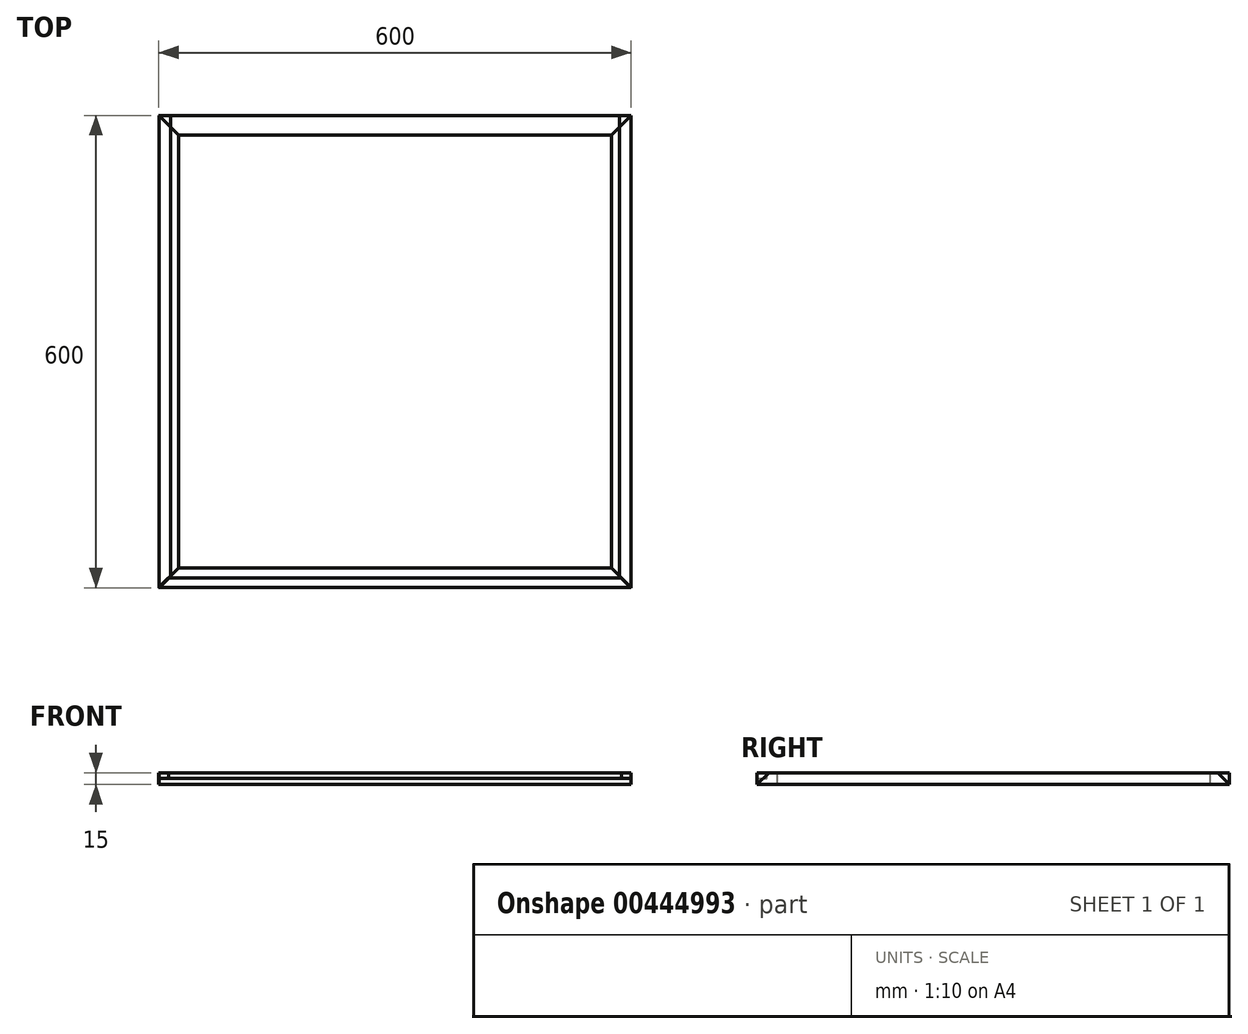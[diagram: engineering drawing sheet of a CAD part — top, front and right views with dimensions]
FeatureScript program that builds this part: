
annotation { "Feature Type Name" : "Feature", "Feature Type Description" : "" }
export const myFeature = defineFeature(function(context is Context, id is Id, definition is map)
    precondition{}
    {
        {
            var Q0;
            Q0=qCreatedBy(makeId("Front.planeOp"),FACE);
            var sketch = newSketch(context, id + "F0", { "sketchPlane" : qUnion([Q0])});
            skLineSegment(sketch, "E0.bottom", {"start": v(0, 0) * mm, "end": v(25, 0) * mm});
            skLineSegment(sketch, "E0.top", {"start": v(0, 15) * mm, "end": v(25, 15) * mm});
            skLineSegment(sketch, "E0.left", {"start": v(0, 0) * mm, "end": v(0, 15) * mm});
            skLineSegment(sketch, "E0.right", {"start": v(25, 0) * mm, "end": v(25, 15) * mm});
            skSolve(sketch);
        }
        {
            var Q0;
            Q0=makeQuery(id+"F0.imprint","IMPRINT",FACE,{"disambiguationData":[TD([[makeQuery(id+"F0.imprint","IMPRINT",EDGE,{"derivedFrom":sQuery(id+"F0.wireOp",EDGE,"E0.bottom")}),1.0]])]});
            extrude(context, id + "F1", {"entities" : qUnion([Q0]), "endBound" : BoundingType.SYMMETRIC, "depth" : 600 * mm});
        }
        {
            var Q0;
            Q0=makeQuery(id+"F1.opExtrude","SWEPT_FACE",FACE,{"disambiguationData":[OSD([sQuery(id+"F0.wireOp",EDGE,"E0.bottom")])]});
            var sketch = newSketch(context, id + "F2", { "sketchPlane" : qUnion([Q0])});
            skLineSegment(sketch, "E1", {"start": v(25, 300) * mm, "end": v(0, 275) * mm});
            skLineSegment(sketch, "E2", {"start": v(0, 275) * mm, "end": v(0, 300) * mm});
            skLineSegment(sketch, "E3", {"start": v(0, 300) * mm, "end": v(25, 300) * mm});
            skLineSegment(sketch, "E4.MirrorCS", {"start": v(25, -300) * mm, "end": v(0, -275) * mm});
            skLineSegment(sketch, "E5.MirrorCS", {"start": v(0, -300) * mm, "end": v(25, -300) * mm});
            skLineSegment(sketch, "E6.MirrorCS", {"start": v(0, -275) * mm, "end": v(0, -300) * mm});
            skSolve(sketch);
        }
        {
            var Q0;
            Q0=makeQuery(id+"F2.imprint","IMPRINT",FACE,{"disambiguationData":[TD([[makeQuery(id+"F2.imprint","IMPRINT",EDGE,{"derivedFrom":sQuery(id+"F2.wireOp",EDGE,"E1")}),-1.0]])]});
            var Q1;
            Q1=makeQuery(id+"F2.imprint","IMPRINT",FACE,{"disambiguationData":[TD([[makeQuery(id+"F2.imprint","IMPRINT",EDGE,{"derivedFrom":sQuery(id+"F2.wireOp",EDGE,"E4.MirrorCS")}),1.0]])]});
            extrude(context, id + "F3", {"entities" : qUnion([Q0, Q1]), "operationType" : NewBodyOperationType.REMOVE, "endBound" : BoundingType.SYMMETRIC, "oppositeDirection" : true, "depth" : 60 * mm});
        }
        {
            var Q0;
            Q0=qCreatedBy(makeId("Front.planeOp"),FACE);
            var sketch = newSketch(context, id + "F4", { "sketchPlane" : qUnion([Q0])});
            skLineSegment(sketch, "E7", {"start": v(-274.97, 0) * mm, "end": v(-274.97, -161.43) * mm, "construction": true});
            skSolve(sketch);
        }
        {
            var Q0;
            Q0=makeQuery(id+"F1.opExtrude","SWEPT_BODY",BODY,{"disambiguationData":[OSD([sQuery(id+"F0.wireOp",EDGE,"E0.bottom"),sQuery(id+"F0.wireOp",EDGE,"E0.top"),sQuery(id+"F0.wireOp",EDGE,"E0.left"),sQuery(id+"F0.wireOp",EDGE,"E0.right")])]});
            var Q1;
            Q1=sQuery(id+"F4.wireOp",EDGE,"E7");
            circularPattern(context, id + "F5", {"entities" : qUnion([Q0]), "axis" : qUnion([Q1]), "angle" : 360 * degree, "instanceCount" : 4, "equalSpace" : true});
        }
        {
            var Q0;
            Q0=makeQuery(id+"F5.opPattern","COPY",FACE,{"derivedFrom":makeQuery(id+"F1.opExtrude","SWEPT_FACE",FACE,{"disambiguationData":[OSD([sQuery(id+"F0.wireOp",EDGE,"E0.left")])]}),"instanceName":"2"});
            var Q1;
            Q1=makeQuery(id+"F1.opExtrude","SWEPT_FACE",FACE,{"disambiguationData":[OSD([sQuery(id+"F0.wireOp",EDGE,"E0.left")])]});
            extrude(context, id + "F6", {"entities" : qUnion([Q0]), "endBound" : BoundingType.UP_TO_SURFACE, "endBoundEntityFace" : qUnion([Q1]), "depth" : 25 * mm});
        }
        {
            var Q0;
            Q0=makeQuery(id+"F5.opPattern","COPY",FACE,{"derivedFrom":makeQuery(id+"F1.opExtrude","SWEPT_FACE",FACE,{"disambiguationData":[OSD([sQuery(id+"F0.wireOp",EDGE,"E0.right")])]}),"instanceName":"2"});
            var Q1;
            Q1=makeQuery(id+"F1.opExtrude","SWEPT_FACE",FACE,{"disambiguationData":[OSD([sQuery(id+"F0.wireOp",EDGE,"E0.right")])]});
            cPlane(context, id + "F7", {"entities" : qUnion([Q0, Q1]), "cplaneType" : CPlaneType.MID_PLANE, "offset" : 25 * mm, "width" : 150 * mm, "height" : 150 * mm});
        }
        {
            var Q0;
            Q0=qCreatedBy(id+"F7.planeOp",FACE);
            var sketch = newSketch(context, id + "F8", { "sketchPlane" : qUnion([Q0])});
            skLineSegment(sketch, "E8", {"start": v(299.97, 7.5) * mm, "end": v(287.47, 7.5) * mm});
            skLineSegment(sketch, "E9", {"start": v(287.47, 7.5) * mm, "end": v(287.47, 15) * mm});
            skLineSegment(sketch, "E10", {"start": v(287.47, 15) * mm, "end": v(299.97, 15) * mm});
            skLineSegment(sketch, "E11", {"start": v(299.97, 15) * mm, "end": v(299.97, 7.5) * mm});
            skSolve(sketch);
        }
        {
            var Q0;
            Q0 = qSketchRegion(id + "F8", true);
            var Q1;
            Q1=makeQuery(id+"F5.opPattern","COPY",BODY,{"derivedFrom":makeQuery(id+"F1.opExtrude","SWEPT_BODY",BODY,{"disambiguationData":[OSD([sQuery(id+"F0.wireOp",EDGE,"E0.bottom"),sQuery(id+"F0.wireOp",EDGE,"E0.top"),sQuery(id+"F0.wireOp",EDGE,"E0.left"),sQuery(id+"F0.wireOp",EDGE,"E0.right")])]}),"instanceName":"2"});
            extrude(context, id + "F9", {"entities" : qUnion([Q0]), "operationType" : NewBodyOperationType.REMOVE, "endBound" : BoundingType.UP_TO_BODY, "endBoundEntityBody" : qUnion([Q1]), "depth" : 25 * mm});
        }
        {
            var Q0;
            Q0 = qSketchRegion(id + "F8", true);
            var Q1;
            Q1=makeQuery(id+"F1.opExtrude","SWEPT_BODY",BODY,{"disambiguationData":[OSD([sQuery(id+"F0.wireOp",EDGE,"E0.bottom"),sQuery(id+"F0.wireOp",EDGE,"E0.top"),sQuery(id+"F0.wireOp",EDGE,"E0.left"),sQuery(id+"F0.wireOp",EDGE,"E0.right")])]});
            extrude(context, id + "F10", {"entities" : qUnion([Q0]), "operationType" : NewBodyOperationType.REMOVE, "endBound" : BoundingType.UP_TO_BODY, "oppositeDirection" : true, "endBoundEntityBody" : qUnion([Q1]), "depth" : 25 * mm});
        }
        {
            var Q0;
            Q0=qCreatedBy(makeId("Front.planeOp"),FACE);
            var sketch = newSketch(context, id + "F11", { "sketchPlane" : qUnion([Q0])});
            skLineSegment(sketch, "E12", {"start": v(-574.95, 0) * mm, "end": v(-559.95, 15) * mm});
            skLineSegment(sketch, "E13", {"start": v(-559.95, 15) * mm, "end": v(-574.95, 15) * mm});
            skLineSegment(sketch, "E14", {"start": v(-574.95, 15) * mm, "end": v(-574.95, 0) * mm});
            skLineSegment(sketch, "E15.MirrorCS", {"start": v(10, 15) * mm, "end": v(25, 15) * mm});
            skLineSegment(sketch, "E16.MirrorCS", {"start": v(25, 0) * mm, "end": v(10, 15) * mm});
            skLineSegment(sketch, "E17.MirrorCS", {"start": v(25, 15) * mm, "end": v(25, 0) * mm});
            skSolve(sketch);
        }
        {
            var Q0;
            Q0 = qSketchRegion(id + "F11", true);
            var Q1;
            Q1=makeQuery(id+"F10.boolean.opBoolean","COPY",FACE,{"derivedFrom":makeQuery(id+"F10.opExtrude","CAP_FACE",FACE,{"disambiguationData":[OSD([sQuery(id+"F2.wireOp",EDGE,"E1")])],"isStart":false})});
            var Q2;
            Q2=makeQuery(id+"F5.opPattern","COPY",BODY,{"derivedFrom":makeQuery(id+"F1.opExtrude","SWEPT_BODY",BODY,{"disambiguationData":[OSD([sQuery(id+"F0.wireOp",EDGE,"E0.bottom"),sQuery(id+"F0.wireOp",EDGE,"E0.top"),sQuery(id+"F0.wireOp",EDGE,"E0.left"),sQuery(id+"F0.wireOp",EDGE,"E0.right")])]}),"instanceName":"3"});
            extrude(context, id + "F12", {"entities" : qUnion([Q0]), "operationType" : NewBodyOperationType.REMOVE, "endBound" : BoundingType.UP_TO_NEXT, "endBoundEntityFace" : qUnion([Q1]), "endBoundEntityBody" : qUnion([Q2]), "depth" : 25 * mm});
        }
        {
            var Q0;
            Q0 = qSketchRegion(id + "F11", true);
            extrude(context, id + "F13", {"entities" : qUnion([Q0]), "operationType" : NewBodyOperationType.REMOVE, "endBound" : BoundingType.THROUGH_ALL, "oppositeDirection" : true, "depth" : 25 * mm});
        }
    });
